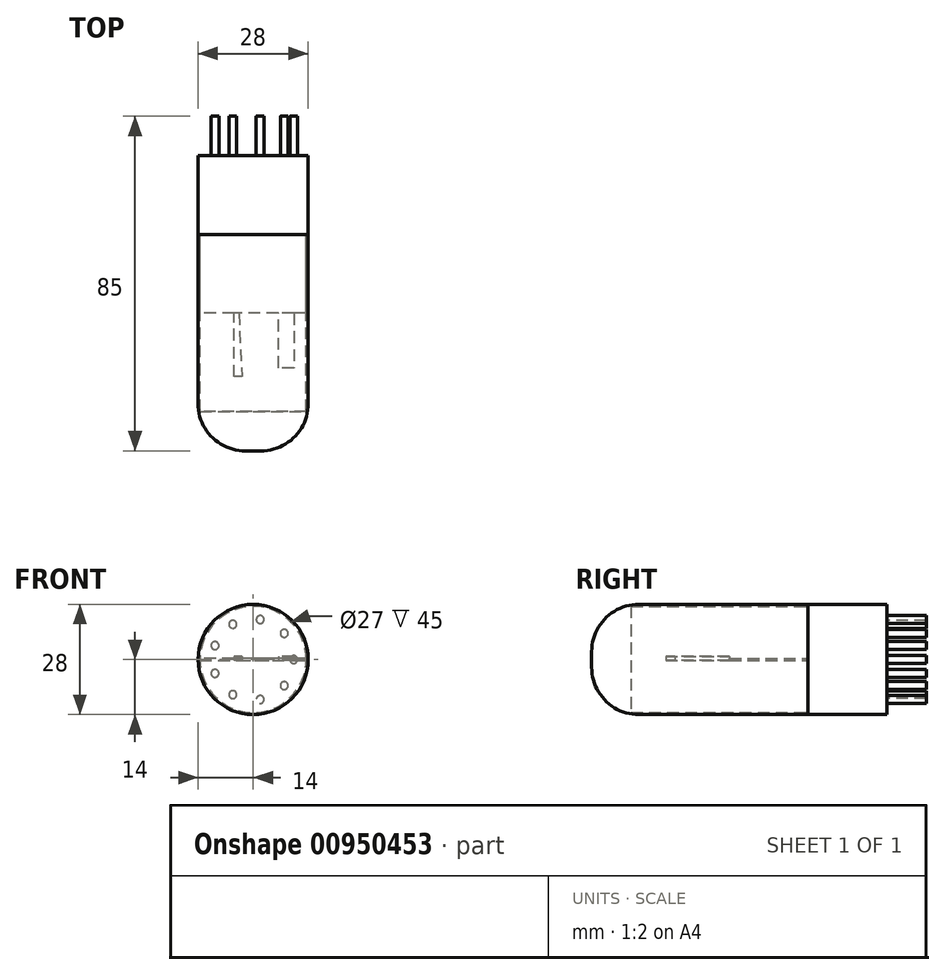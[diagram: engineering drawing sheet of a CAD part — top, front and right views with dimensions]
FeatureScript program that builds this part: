
annotation { "Feature Type Name" : "Feature", "Feature Type Description" : "" }
export const myFeature = defineFeature(function(context is Context, id is Id, definition is map)
    precondition{}
    {
        {
            var Q0;
            Q0=qCreatedBy(makeId("Front.planeOp"),FACE);
            var sketch = newSketch(context, id + "F0", { "sketchPlane" : qUnion([Q0])});
            skCircle(sketch, "E0", {"center": v(0, 0) * mm, "radius": 14 * mm});
            skSolve(sketch);
        }
        {
            var Q0;
            Q0=qSketchRegion(id+"F0",true);
            extrude(context, id + "F1", {"entities" : qUnion([Q0]), "depth" : 25 * mm, "offsetDistance" : 25 * mm});
        }
        {
            var Q0;
            Q0=qSketchRegion(id+"F0",true);
            extrude(context, id + "F2", {"entities" : qUnion([Q0]), "operationType" : NewBodyOperationType.ADD, "depth" : 55 * mm, "offsetDistance" : 25 * mm});
        }
        {
            var Q0;
            Q0=makeQuery(id+"F2.opExtrude","CAP_FACE",FACE,{"disambiguationData":[OSD([sQuery(id+"F0.wireOp",EDGE,"E0")])],"isStart":false});
            fillet(context, id + "F3", {"entities" : qUnion([Q0]), "radius" : 12 * mm, "tangentPropagation" : true, "allowEdgeOverflow" : false});
        }
        {
            var Q0;
            Q0=makeQuery(id+"F1.opExtrude","CAP_FACE",FACE,{"disambiguationData":[OSD([sQuery(id+"F0.wireOp",EDGE,"E0")])],"isStart":true});
            var sketch = newSketch(context, id + "F4", { "sketchPlane" : qUnion([Q0])});
            skCircle(sketch, "E1", {"center": v(0, 0) * mm, "radius": 13.5 * mm});
            skSolve(sketch);
        }
        {
            var Q0;
            Q0=makeQuery(id+"F4.imprint","IMPRINT",FACE,{"disambiguationData":[TD([[makeQuery(id+"F4.imprint","IMPRINT",EDGE,{"derivedFrom":sQuery(id+"F4.wireOp",EDGE,"E1")}),1.0]])]});
            extrude(context, id + "F5", {"entities" : qUnion([Q0]), "operationType" : NewBodyOperationType.REMOVE, "oppositeDirection" : true, "depth" : 45 * mm, "offsetDistance" : 25 * mm});
        }
        {
            var Q0;
            Q0=makeQuery(id+"F1.opExtrude","CAP_FACE",FACE,{"disambiguationData":[OSD([sQuery(id+"F0.wireOp",EDGE,"E0")])],"isStart":true});
            var sketch = newSketch(context, id + "F6", { "sketchPlane" : qUnion([Q0])});
            skLineSegment(sketch, "E2", {"start": v(-13.5, 0.25) * mm, "end": v(13.5, 0.25) * mm});
            skLineSegment(sketch, "E3", {"start": v(-12.06, -0.25) * mm, "end": v(-13.5, -0.25) * mm});
            skLineSegment(sketch, "E4", {"start": v(-13.5, -0.25) * mm, "end": v(-12.06, -0.25) * mm});
            skLineSegment(sketch, "E5", {"start": v(-12.06, -0.25) * mm, "end": v(13.5, -0.25) * mm});
            skSolve(sketch);
        }
        {
            var Q0;
            {var subQ2=sQuery(id+"F6.wireOp",EDGE,"E2");Q0=makeQuery(id+"F6.imprint","IMPRINT",FACE,{"disambiguationData":[TD([[makeQuery(id+"F6.imprint","IMPRINT",EDGE,{"derivedFrom":subQ2}),-1.0]])]});}
            extrude(context, id + "F7", {"entities" : qUnion([Q0]), "oppositeDirection" : true, "depth" : 20 * mm, "offsetDistance" : 25 * mm});
        }
        {
            var Q0;
            Q0=makeQuery(id+"F7.opExtrude","SWEPT_FACE",FACE,{"disambiguationData":[OSD([sQuery(id+"F6.wireOp",EDGE,"E2")])]});
            var sketch = newSketch(context, id + "F8", { "sketchPlane" : qUnion([Q0])});
            skLineSegment(sketch, "E6", {"start": v(10.4, -20) * mm, "end": v(10.4, -33.88) * mm});
            skLineSegment(sketch, "E7", {"start": v(10.4, -33.88) * mm, "end": v(6.4, -33.88) * mm});
            skLineSegment(sketch, "E8", {"start": v(6.4, -33.88) * mm, "end": v(6.4, -20) * mm});
            skLineSegment(sketch, "E9", {"start": v(-3.6, -20) * mm, "end": v(-2.88, -36.07) * mm});
            skLineSegment(sketch, "E10", {"start": v(-2.88, -36.07) * mm, "end": v(-4.8, -36.16) * mm});
            skLineSegment(sketch, "E11", {"start": v(-4.8, -36.16) * mm, "end": v(-4.8, -20) * mm});
            skLineSegment(sketch, "E12", {"start": v(6.4, -20) * mm, "end": v(10.4, -20) * mm});
            skLineSegment(sketch, "E13", {"start": v(-3.6, -20) * mm, "end": v(-4.8, -20) * mm});
            skSolve(sketch);
        }
        {
            var Q0;
            Q0=qSketchRegion(id+"F8",true);
            extrude(context, id + "F9", {"entities" : qUnion([Q0]), "operationType" : NewBodyOperationType.ADD, "depth" : 1 * mm, "hasOffset" : true, "offsetDistance" : 25 * mm, "offsetOppositeDirection" : true, "symmetric" : true});
        }
        {
            var Q0;
            Q0=makeQuery(id+"F0.imprint","IMPRINT",FACE,{"disambiguationData":[TD([[makeQuery(id+"F0.imprint","IMPRINT",EDGE,{"derivedFrom":sQuery(id+"F0.wireOp",EDGE,"E0")}),1.0]])]});
            var sketch = newSketch(context, id + "F10", { "sketchPlane" : qUnion([Q0])});
            skCircle(sketch, "E14", {"center": v(0, 0) * mm, "radius": 14 * mm});
            skSolve(sketch);
        }
        {
            var Q0;
            Q0=qSketchRegion(id+"F10",true);
            extrude(context, id + "F11", {"entities" : qUnion([Q0]), "oppositeDirection" : true, "depth" : 20 * mm, "offsetDistance" : 25 * mm});
        }
        {
            var Q0;
            Q0=makeQuery(id+"F11.opExtrude","CAP_FACE",FACE,{"disambiguationData":[OSD([sQuery(id+"F10.wireOp",EDGE,"E14")])],"isStart":false});
            var sketch = newSketch(context, id + "F12", { "sketchPlane" : qUnion([Q0])});
            skPoint(sketch, "E15.0.midPoint", {"position": v(9.69, 0) * mm});
            skCircle(sketch, "E16", {"center": v(-1.8, -10.15) * mm, "radius": 1 * mm});
            skCircle(sketch, "E17", {"center": v(5.16, -8.93) * mm, "radius": 1 * mm});
            skCircle(sketch, "E18", {"center": v(9.69, -3.53) * mm, "radius": 1 * mm});
            skCircle(sketch, "E19", {"center": v(9.69, 3.53) * mm, "radius": 1 * mm});
            skCircle(sketch, "E20", {"center": v(5.16, 8.93) * mm, "radius": 1 * mm});
            skCircle(sketch, "E21", {"center": v(-1.8, 10.15) * mm, "radius": 1 * mm});
            skCircle(sketch, "E22", {"center": v(-7.9, 6.63) * mm, "radius": 1 * mm});
            skCircle(sketch, "E23", {"center": v(-10.31, 0) * mm, "radius": 1 * mm});
            skCircle(sketch, "E24", {"center": v(-7.9, -6.63) * mm, "radius": 1 * mm});
            skSolve(sketch);
        }
        {
            var Q0;
            Q0=makeQuery(id+"F12.imprint","IMPRINT",FACE,{"disambiguationData":[TD([[makeQuery(id+"F12.imprint","IMPRINT",EDGE,{"derivedFrom":sQuery(id+"F12.wireOp",EDGE,"E17")}),1.0]])]});
            var Q1;
            Q1=makeQuery(id+"F12.imprint","IMPRINT",FACE,{"disambiguationData":[TD([[makeQuery(id+"F12.imprint","IMPRINT",EDGE,{"derivedFrom":sQuery(id+"F12.wireOp",EDGE,"E18")}),1.0]])]});
            var Q2;
            Q2=makeQuery(id+"F12.imprint","IMPRINT",FACE,{"disambiguationData":[TD([[makeQuery(id+"F12.imprint","IMPRINT",EDGE,{"derivedFrom":sQuery(id+"F12.wireOp",EDGE,"E19")}),1.0]])]});
            var Q3;
            Q3=makeQuery(id+"F12.imprint","IMPRINT",FACE,{"disambiguationData":[TD([[makeQuery(id+"F12.imprint","IMPRINT",EDGE,{"derivedFrom":sQuery(id+"F12.wireOp",EDGE,"E20")}),1.0]])]});
            var Q4;
            Q4=makeQuery(id+"F12.imprint","IMPRINT",FACE,{"disambiguationData":[TD([[makeQuery(id+"F12.imprint","IMPRINT",EDGE,{"derivedFrom":sQuery(id+"F12.wireOp",EDGE,"E21")}),1.0]])]});
            var Q5;
            Q5=makeQuery(id+"F12.imprint","IMPRINT",FACE,{"disambiguationData":[TD([[makeQuery(id+"F12.imprint","IMPRINT",EDGE,{"derivedFrom":sQuery(id+"F12.wireOp",EDGE,"E22")}),1.0]])]});
            var Q6;
            Q6=makeQuery(id+"F12.imprint","IMPRINT",FACE,{"disambiguationData":[TD([[makeQuery(id+"F12.imprint","IMPRINT",EDGE,{"derivedFrom":sQuery(id+"F12.wireOp",EDGE,"E23")}),1.0]])]});
            var Q7;
            Q7=makeQuery(id+"F12.imprint","IMPRINT",FACE,{"disambiguationData":[TD([[makeQuery(id+"F12.imprint","IMPRINT",EDGE,{"derivedFrom":sQuery(id+"F12.wireOp",EDGE,"E24")}),1.0]])]});
            var Q8;
            Q8=makeQuery(id+"F12.imprint","IMPRINT",FACE,{"disambiguationData":[TD([[makeQuery(id+"F12.imprint","IMPRINT",EDGE,{"derivedFrom":sQuery(id+"F12.wireOp",EDGE,"E16")}),1.0]])]});
            extrude(context, id + "F13", {"entities" : qUnion([Q0, Q1, Q2, Q3, Q4, Q5, Q6, Q7, Q8]), "operationType" : NewBodyOperationType.ADD, "depth" : 10 * mm, "offsetDistance" : 25 * mm});
        }
    });
